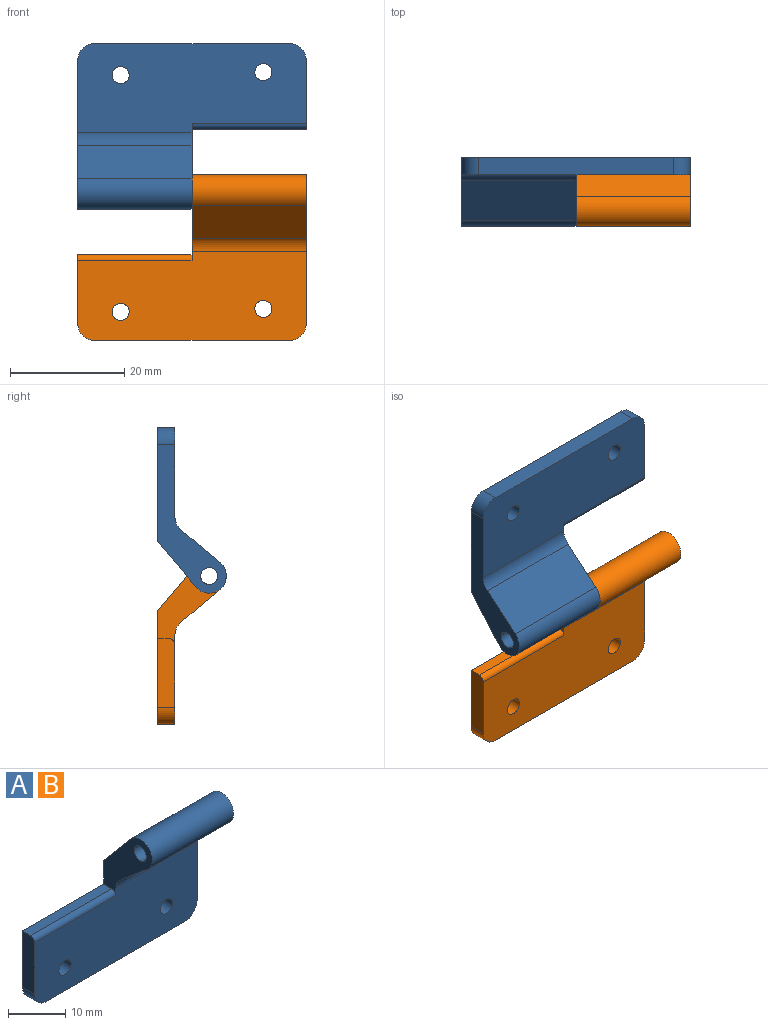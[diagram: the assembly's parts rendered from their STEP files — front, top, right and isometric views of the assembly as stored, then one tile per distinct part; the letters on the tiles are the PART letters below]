
ASSEMBLY  parts=2 mates=1
PART A: 17 faces, bbox 40x12x29 mm
  f0: plane 12x3mm, normal (-1,0,0), area 35.8mm2, adj f2,f4,f5,f12,f15
  f1: plane 34x3mm, normal (0,0,-1), area 102mm2, adj f4,f5,f14,f15
  f2: plane 20x2mm, normal (0,0,1), area 40mm2, adj f0,f5,f11,f12
  f3: cylinder r=1.5mm len=3mm, axis (0,1,0), area 28.3mm2, adj f4,f5
  f4: plane 40x15.61mm, normal (0,-1,0), area 574.2mm2, adj f0,f1,f3,f10,f11,f12,f13,f14
  f5: plane 40x20mm, normal (0,1,0), area 682mm2, adj f0,f1,f2,f3,f6,f10,f11,f14
  f6: plane 20x7.94mm, normal (0,0.76,0.65), area 207.8mm2, adj f5,f7,f10,f11
  f7: cylinder r=3mm len=20mm, axis (-1,0,0), area 198.5mm2, adj f6,f8,f10,f11
  f8: plane 20x6.87mm, normal (0,-0.65,-0.76), area 180mm2, adj f7,f10,f11,f13
  f9: cylinder r=1.5mm len=20mm, axis (-1,0,0), area 188.5mm2, adj f10,f11
  f10: plane 26x12mm, normal (1,0,0), area 108.3mm2, adj f4,f5,f6,f7,f8,f9,f13,f14
  f11: plane 15x12mm, normal (-1,0,0), area 72.5mm2, adj f2,f4,f5,f6,f7,f8,f9,f12
  f12: cylinder r=1mm len=20mm, axis (1,0,0), area 31.4mm2, adj f0,f2,f4,f11
  f13: cylinder r=3mm len=20mm, axis (1,0,0), area 52.1mm2, adj f4,f8,f10,f11
  f14: cylinder r=3mm len=3mm, axis (0,-1,0), area 14.1mm2, adj f1,f4,f5,f10
  f15: cylinder r=3mm len=3mm, axis (0,-1,0), area 14.1mm2, adj f0,f1,f4,f5
  f16: cylinder r=1.5mm len=3mm, axis (0,-1,0), area 28.3mm2, adj f4,f5
PART B: same geometry as A
PLACE A rot(axis=(0,1,0),180deg) t=(3,0,52)mm
PLACE B t=(-37,0,0)mm
MATE revolute B.f7 <-> A.f7  axis (-1,0,0) through (-17,-9,26)mm
